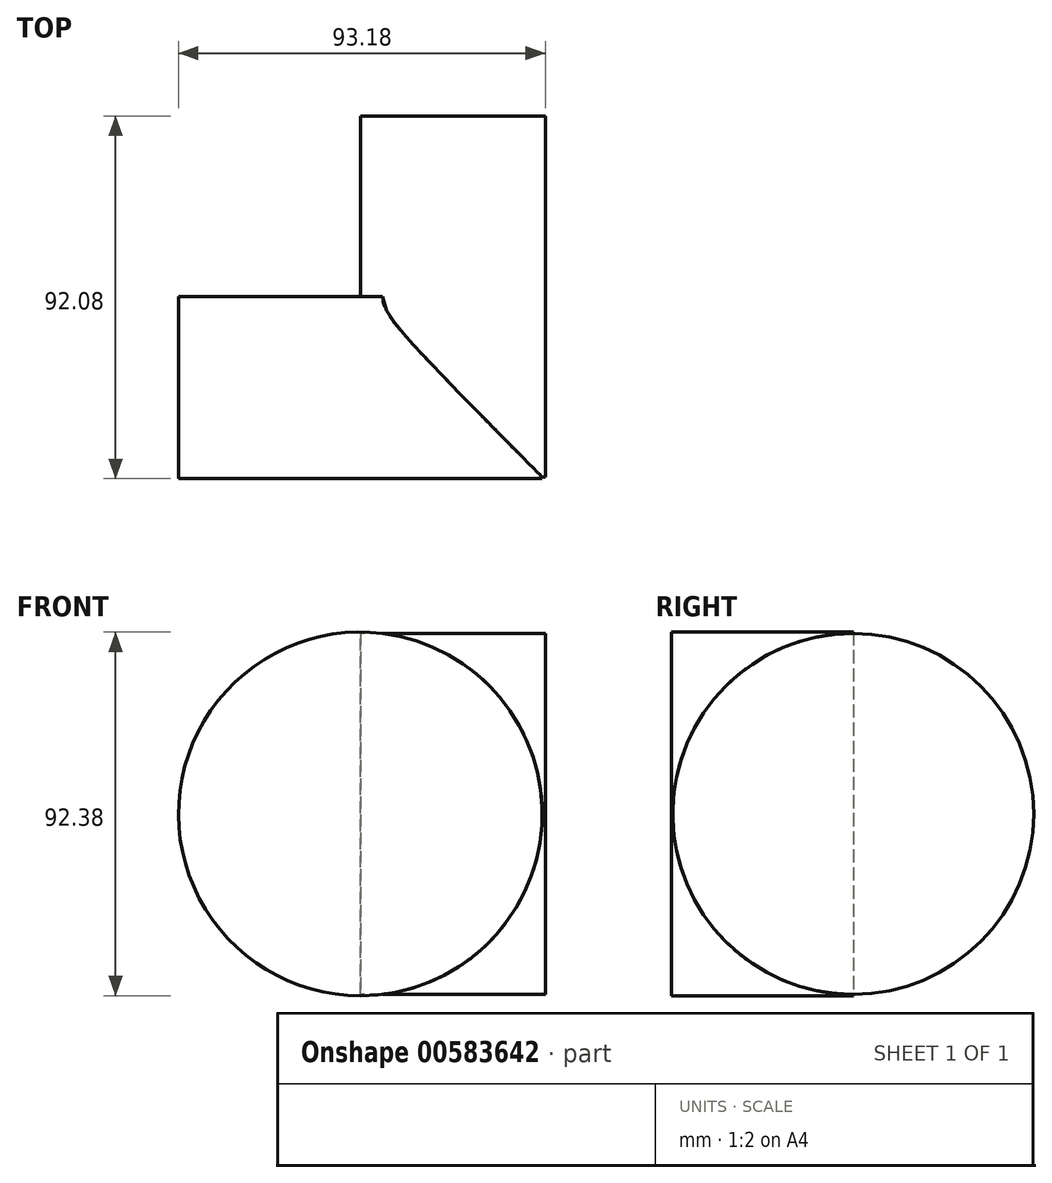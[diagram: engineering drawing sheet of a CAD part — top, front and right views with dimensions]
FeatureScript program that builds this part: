
annotation { "Feature Type Name" : "Feature", "Feature Type Description" : "" }
export const myFeature = defineFeature(function(context is Context, id is Id, definition is map)
    precondition{}
    {
        {
            var Q0;
            Q0=qCreatedBy(makeId("Front.planeOp"),FACE);
            var sketch = newSketch(context, id + "F0", { "sketchPlane" : qUnion([Q0])});
            skCircle(sketch, "E0", {"center": v(0, 0) * mm, "radius": 46.19 * mm});
            skSolve(sketch);
        }
        {
            var Q0;
            Q0=qCreatedBy(makeId("Right.planeOp"),FACE);
            var sketch = newSketch(context, id + "F1", { "sketchPlane" : qUnion([Q0])});
            skCircle(sketch, "E1", {"center": v(0, 0) * mm, "radius": 45.85 * mm});
            skSolve(sketch);
        }
        {
            var Q0;
            Q0=makeQuery(id+"F1.imprint","IMPRINT",FACE,{"disambiguationData":[TD([[makeQuery(id+"F1.imprint","IMPRINT",EDGE,{"derivedFrom":sQuery(id+"F1.wireOp",EDGE,"E1")}),1.0]])]});
            extrude(context, id + "F2", {"entities" : qUnion([Q0]), "depth" : 47 * mm, "offsetDistance" : 25.4 * mm});
        }
        {
            var Q0;
            Q0=makeQuery(id+"F0.imprint","IMPRINT",FACE,{"disambiguationData":[TD([[makeQuery(id+"F0.imprint","IMPRINT",EDGE,{"derivedFrom":sQuery(id+"F0.wireOp",EDGE,"E0")}),1.0]])]});
            extrude(context, id + "F3", {"entities" : qUnion([Q0]), "operationType" : NewBodyOperationType.ADD, "depth" : 46.23 * mm, "offsetDistance" : 25.4 * mm});
        }
    });
